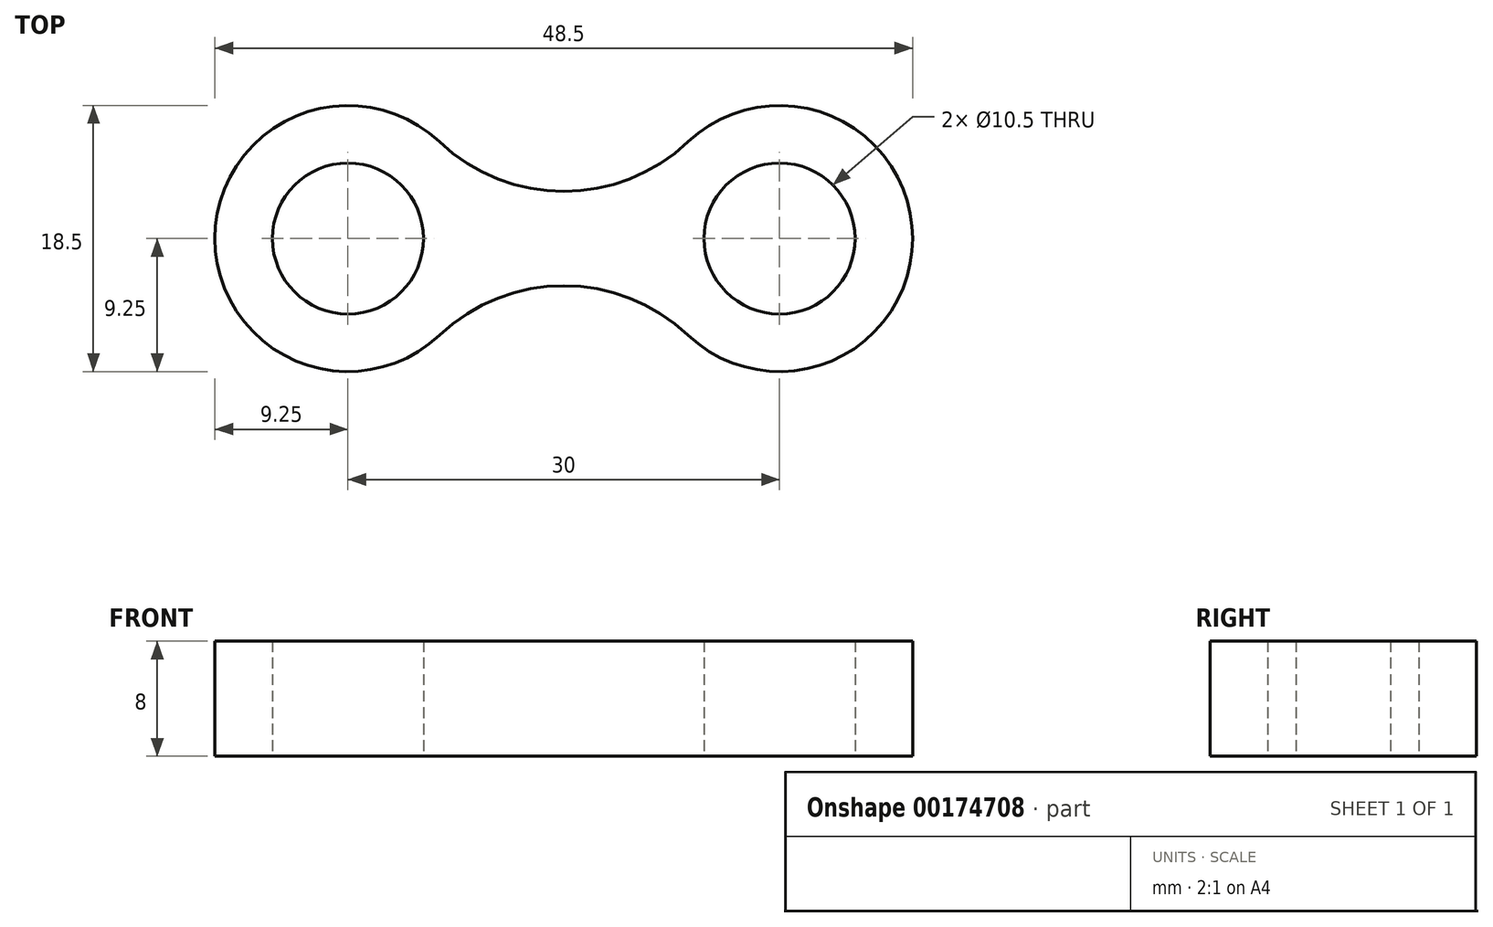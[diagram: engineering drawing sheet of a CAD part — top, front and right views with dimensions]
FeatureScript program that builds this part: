
annotation { "Feature Type Name" : "Feature", "Feature Type Description" : "" }
export const myFeature = defineFeature(function(context is Context, id is Id, definition is map)
    precondition{}
    {
        {
            var Q0;
            Q0=qCreatedBy(makeId("Top.planeOp"),FACE);
            var sketch = newSketch(context, id + "F0", { "sketchPlane" : qUnion([Q0])});
            skCircle(sketch, "E0", {"center": v(0, 0) * mm, "radius": 5.25 * mm});
            skCircle(sketch, "E1", {"center": v(30, 0) * mm, "radius": 5.25 * mm});
            skCircle(sketch, "E2.0", {"center": v(0, 0) * mm, "radius": 9.25 * mm});
            skCircle(sketch, "E3.0", {"center": v(30, 0) * mm, "radius": 9.25 * mm});
            skLineSegment(sketch, "E4", {"start": v(0, 9.25) * mm, "end": v(30, 9.25) * mm});
            skLineSegment(sketch, "E5", {"start": v(0, -9.25) * mm, "end": v(30, -9.25) * mm});
            skPoint(sketch, "E6", {"position": v(15, 9.25) * mm});
            skLineSegment(sketch, "E7", {"start": v(15, 20.19) * mm, "end": v(15, -20.26) * mm, "construction": true});
            skPoint(sketch, "E7.endSnap0", {"position": v(15, -9.25) * mm});
            skCircle(sketch, "E8", {"center": v(15, 15.88) * mm, "radius": 12.6 * mm});
            skCircle(sketch, "E9.MirrorC", {"center": v(15, -15.88) * mm, "radius": 12.6 * mm});
            skSolve(sketch);
        }
        {
            var Q0;
            Q0=makeQuery(id+"F0.imprint","IMPRINT",FACE,{"disambiguationData":[TD([[makeQuery(id+"F0.imprint","IMPRINT",EDGE,{"derivedFrom":sQuery(id+"F0.wireOp",EDGE,"E0")}),-1.0]])]});
            var Q1;
            Q1=makeQuery(id+"F0.imprint","IMPRINT",FACE,{"disambiguationData":[TD([[makeQuery(id+"F0.imprint","IMPRINT",EDGE,{"derivedFrom":sQuery(id+"F0.wireOp",EDGE,"E1")}),-1.0]])]});
            var Q2;
            {var subQ0=sQuery(id+"F0.wireOp",EDGE,"E8");var subQ1=sQuery(id+"F0.wireOp",EDGE,"E2.0");var subQ2=makeQuery(id+"F0.imprint","INTERSECT",VERTEX,{"derivedFrom":[subQ1,subQ0]});Q2=makeQuery(id+"F0.imprint","IMPRINT",FACE,{"disambiguationData":[TD([[makeQuery(id+"F0.imprint","IMPRINT",EDGE,{"disambiguationData":[TD([[subQ2,1.0]])],"derivedFrom":subQ1}),-1.0]])]});}
            extrude(context, id + "F1", {"entities" : qUnion([Q0, Q1, Q2]), "depth" : 8 * mm});
        }
    });
